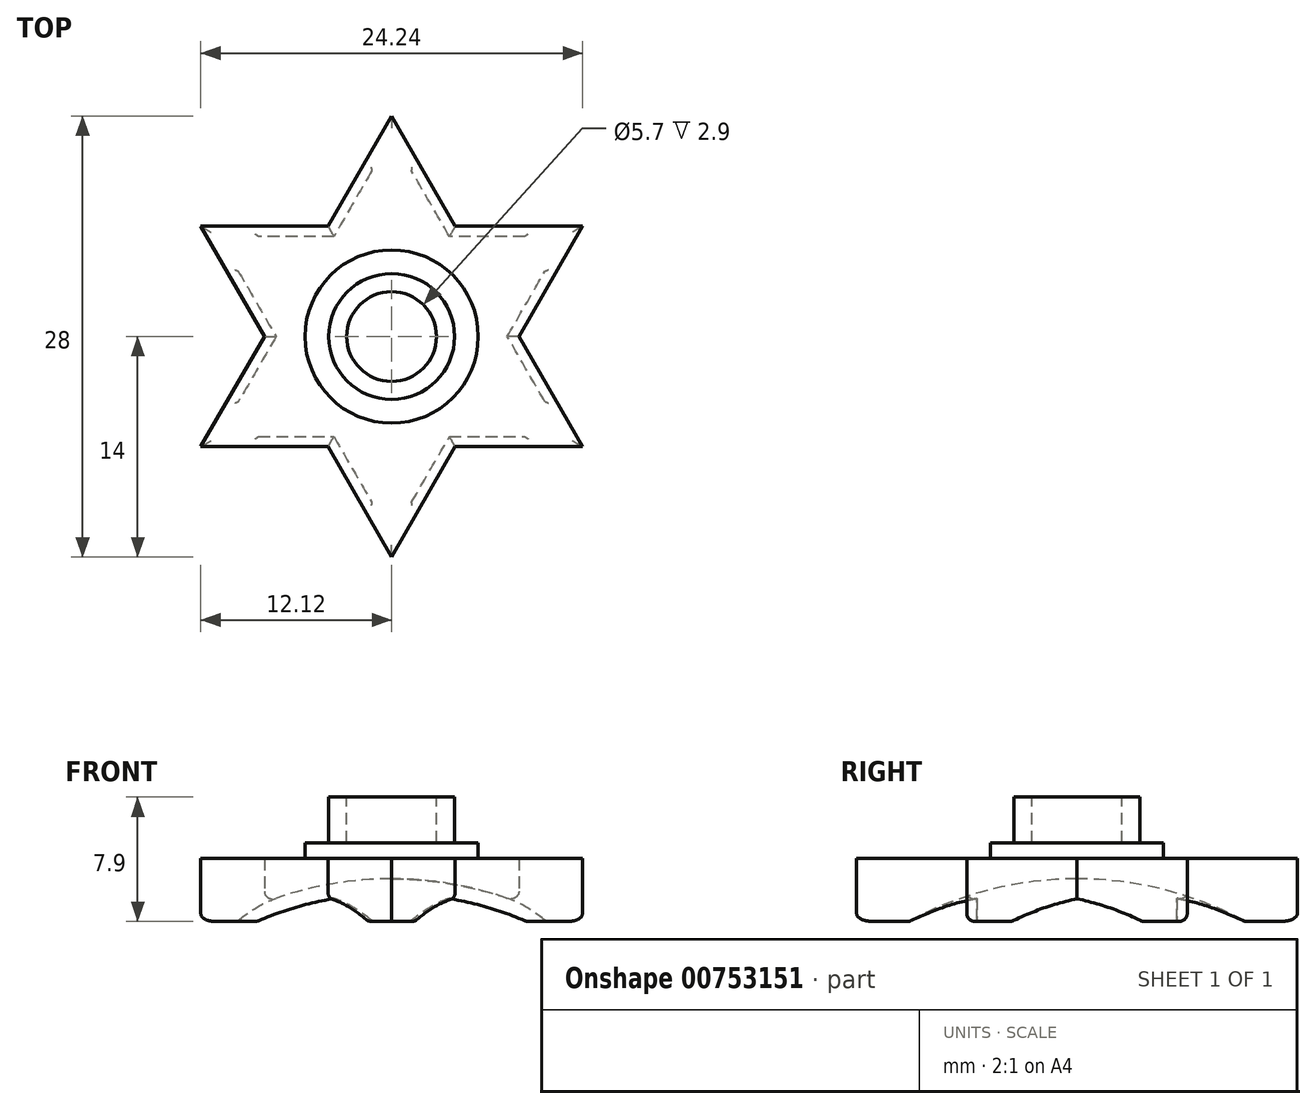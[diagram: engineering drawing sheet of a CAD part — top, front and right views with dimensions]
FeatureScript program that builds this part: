
annotation { "Feature Type Name" : "Feature", "Feature Type Description" : "" }
export const myFeature = defineFeature(function(context is Context, id is Id, definition is map)
    precondition{}
    {
        {
            var Q0;
            Q0=qCreatedBy(makeId("Top.planeOp"),FACE);
            var sketch = newSketch(context, id + "F0", { "sketchPlane" : qUnion([Q0])});
            skCircle(sketch, "E0", {"center": v(0, 0) * mm, "radius": 14 * mm, "construction": true});
            skLineSegment(sketch, "E1", {"start": v(-12.12, 7) * mm, "end": v(12.12, 7) * mm});
            skLineSegment(sketch, "E2", {"start": v(12.12, 7) * mm, "end": v(0, -14) * mm});
            skLineSegment(sketch, "E3", {"start": v(0, -14) * mm, "end": v(-12.12, 7) * mm});
            skLineSegment(sketch, "E4", {"start": v(-12.12, -7) * mm, "end": v(12.12, -7) * mm});
            skLineSegment(sketch, "E5", {"start": v(12.12, -7) * mm, "end": v(0, 14) * mm});
            skLineSegment(sketch, "E6", {"start": v(0, 14) * mm, "end": v(-12.12, -7) * mm});
            skSolve(sketch);
        }
        {
            var Q0;
            Q0=qSketchRegion(id+"F0",true);
            extrude(context, id + "F1", {"entities" : qUnion([Q0]), "depth" : 4 * mm, "offsetDistance" : 25 * mm});
        }
        {
            var Q0;
            Q0=qCreatedBy(makeId("Front.planeOp"),FACE);
            var sketch = newSketch(context, id + "F2", { "sketchPlane" : qUnion([Q0])});
            skLineSegment(sketch, "E7", {"start": v(0, 0) * mm, "end": v(0, -4.5) * mm, "construction": true});
            skSolve(sketch);
        }
        {
            var Q0;
            Q0=qCreatedBy(makeId("Front.planeOp"),FACE);
            var sketch = newSketch(context, id + "F3", { "sketchPlane" : qUnion([Q0])});
            skArc(sketch, "E8", {"start": v(0, 2.7) * mm, "mid": v(-22.55, -19.85) * mm, "end": v(0, -42.4) * mm});
            skLineSegment(sketch, "E9", {"start": v(0, 2.7) * mm, "end": v(0, -42.4) * mm});
            skPoint(sketch, "E10", {"position": v(-10.7, 0) * mm});
            skSolve(sketch);
        }
        {
            var Q0;
            Q0=qSketchRegion(id+"F3",true);
            var Q1;
            Q1=sQuery(id+"F3.wireOp",EDGE,"E9");
            revolve(context, id + "F4", {"operationType" : NewBodyOperationType.REMOVE, "surfaceOperationType" : NewSurfaceOperationType.NEW, "entities" : qUnion([Q0]), "axis" : qUnion([Q1]), "revolveType" : RevolveType.FULL, "oppositeDirection" : true});
        }
        {
            var Q0;
            Q0=makeQuery(id+"F1.opExtrude","CAP_FACE",FACE,{"disambiguationData":[OSD([sQuery(id+"F0.wireOp",EDGE,"E1"),sQuery(id+"F0.wireOp",EDGE,"E2"),sQuery(id+"F0.wireOp",EDGE,"E3"),sQuery(id+"F0.wireOp",EDGE,"E4"),sQuery(id+"F0.wireOp",EDGE,"E5"),sQuery(id+"F0.wireOp",EDGE,"E6")])],"isStart":false});
            var sketch = newSketch(context, id + "F5", { "sketchPlane" : qUnion([Q0])});
            skCircle(sketch, "E11", {"center": v(0, 0) * mm, "radius": 5.5 * mm});
            skSolve(sketch);
        }
        {
            var Q0;
            Q0=qSketchRegion(id+"F5",true);
            extrude(context, id + "F6", {"entities" : qUnion([Q0]), "operationType" : NewBodyOperationType.ADD, "depth" : 1 * mm, "offsetDistance" : 25 * mm});
        }
        {
            var Q0;
            Q0=makeQuery(id+"F6.opExtrude","CAP_FACE",FACE,{"disambiguationData":[OSD([sQuery(id+"F5.wireOp",EDGE,"E11")])],"isStart":false});
            var sketch = newSketch(context, id + "F7", { "sketchPlane" : qUnion([Q0])});
            skCircle(sketch, "E12", {"center": v(0, 0) * mm, "radius": 4 * mm});
            skSolve(sketch);
        }
        {
            var Q0;
            Q0=qSketchRegion(id+"F7",true);
            extrude(context, id + "F8", {"entities" : qUnion([Q0]), "operationType" : NewBodyOperationType.ADD, "depth" : 2.9 * mm, "offsetDistance" : 25 * mm});
        }
        {
            var Q0;
            Q0=makeQuery(id+"F8.opExtrude","CAP_FACE",FACE,{"disambiguationData":[OSD([sQuery(id+"F7.wireOp",EDGE,"E12")])],"isStart":false});
            var sketch = newSketch(context, id + "F9", { "sketchPlane" : qUnion([Q0])});
            skCircle(sketch, "E13", {"center": v(0, 0) * mm, "radius": 2.85 * mm});
            skSolve(sketch);
        }
        {
            var Q0;
            Q0=qSketchRegion(id+"F9",true);
            extrude(context, id + "F10", {"entities" : qUnion([Q0]), "operationType" : NewBodyOperationType.REMOVE, "oppositeDirection" : true, "depth" : 2.9 * mm, "offsetDistance" : 25 * mm});
        }
        {
            var Q0;
            Q0=makeQuery(id+"F1.opExtrude","CAP_EDGE",EDGE,{"disambiguationData":[OSD([sQuery(id+"F0.wireOp",EDGE,"1e846c76-ade1-459f-9f20-eea542154bc1.trimOffspring")])],"isStart":true});
            var Q1;
            Q1=makeQuery(id+"F4.boolean.opBoolean","INTERSECT",EDGE,{"disambiguationData":[OD(1.0)],"derivedFrom":[makeQuery(id+"F1.opExtrude","SWEPT_FACE",FACE,{"disambiguationData":[OSD([sQuery(id+"F0.wireOp",EDGE,"1e846c76-ade1-459f-9f20-eea542154bc1.trimOffspring")])]}),makeQuery(id+"F4.opRevolve","SWEPT_FACE",FACE,{"disambiguationData":[OSD([sQuery(id+"F3.wireOp",EDGE,"E8")])]})]});
            var Q2;
            Q2=makeQuery(id+"F4.boolean.opBoolean","INTERSECT",EDGE,{"disambiguationData":[OD(1.0)],"derivedFrom":[makeQuery(id+"F1.opExtrude","SWEPT_FACE",FACE,{"disambiguationData":[OSD([sQuery(id+"F0.wireOp",EDGE,"tKFEvPMP-PRdD-FNsb-sHzV-FJ5KZ0vE21vF")])]}),makeQuery(id+"F4.opRevolve","SWEPT_FACE",FACE,{"disambiguationData":[OSD([sQuery(id+"F3.wireOp",EDGE,"E8")])]})]});
            var Q3;
            Q3=makeQuery(id+"F1.opExtrude","CAP_EDGE",EDGE,{"disambiguationData":[OSD([sQuery(id+"F0.wireOp",EDGE,"tKFEvPMP-PRdD-FNsb-sHzV-FJ5KZ0vE21vF")])],"isStart":true});
            var Q4;
            {var subQ0=sQuery(id+"F0.wireOp",EDGE,"E6");Q4=makeQuery(id+"F1.opExtrude","CAP_EDGE",EDGE,{"disambiguationData":[OSD([subQ0]),TDD([makeQuery(id+"F0.imprint","IMPRINT",EDGE,{"disambiguationData":[TD([[makeQuery(id+"F0.imprint","INTERSECT",VERTEX,{"derivedFrom":[sQuery(id+"F0.wireOp",EDGE,"E4"),subQ0]}),1.0]])],"derivedFrom":subQ0})])],"isStart":true});}
            var Q5;
            {var subQ0=sQuery(id+"F0.wireOp",EDGE,"E4");Q5=makeQuery(id+"F1.opExtrude","CAP_EDGE",EDGE,{"disambiguationData":[OSD([subQ0]),TDD([makeQuery(id+"F0.imprint","IMPRINT",EDGE,{"disambiguationData":[TD([[makeQuery(id+"F0.imprint","INTERSECT",VERTEX,{"derivedFrom":[subQ0,sQuery(id+"F0.wireOp",EDGE,"E6")]}),-1.0]])],"derivedFrom":subQ0})])],"isStart":true});}
            var Q6;
            {var subQ0=sQuery(id+"F0.wireOp",EDGE,"E3");Q6=makeQuery(id+"F1.opExtrude","CAP_EDGE",EDGE,{"disambiguationData":[OSD([subQ0]),TDD([makeQuery(id+"F0.imprint","IMPRINT",EDGE,{"disambiguationData":[TD([[makeQuery(id+"F0.imprint","INTERSECT",VERTEX,{"derivedFrom":[sQuery(id+"F0.wireOp",EDGE,"E2"),subQ0]}),-1.0]])],"derivedFrom":subQ0})])],"isStart":true});}
            var Q7;
            {var subQ0=sQuery(id+"F0.wireOp",EDGE,"E2");Q7=makeQuery(id+"F1.opExtrude","CAP_EDGE",EDGE,{"disambiguationData":[OSD([subQ0]),TDD([makeQuery(id+"F0.imprint","IMPRINT",EDGE,{"disambiguationData":[TD([[makeQuery(id+"F0.imprint","INTERSECT",VERTEX,{"derivedFrom":[subQ0,sQuery(id+"F0.wireOp",EDGE,"E3")]}),1.0]])],"derivedFrom":subQ0})])],"isStart":true});}
            var Q8;
            {var subQ0=sQuery(id+"F0.wireOp",EDGE,"E4");Q8=makeQuery(id+"F1.opExtrude","CAP_EDGE",EDGE,{"disambiguationData":[OSD([subQ0]),TDD([makeQuery(id+"F0.imprint","IMPRINT",EDGE,{"disambiguationData":[TD([[makeQuery(id+"F0.imprint","INTERSECT",VERTEX,{"derivedFrom":[subQ0,sQuery(id+"F0.wireOp",EDGE,"E5")]}),1.0]])],"derivedFrom":subQ0})])],"isStart":true});}
            var Q9;
            {var subQ0=sQuery(id+"F0.wireOp",EDGE,"E2");Q9=makeQuery(id+"F1.opExtrude","CAP_EDGE",EDGE,{"disambiguationData":[OSD([subQ0]),TDD([makeQuery(id+"F0.imprint","IMPRINT",EDGE,{"disambiguationData":[TD([[makeQuery(id+"F0.imprint","INTERSECT",VERTEX,{"derivedFrom":[sQuery(id+"F0.wireOp",EDGE,"E1"),subQ0]}),-1.0]])],"derivedFrom":subQ0})])],"isStart":true});}
            var Q10;
            {var subQ0=sQuery(id+"F0.wireOp",EDGE,"E1");Q10=makeQuery(id+"F1.opExtrude","CAP_EDGE",EDGE,{"disambiguationData":[OSD([subQ0]),TDD([makeQuery(id+"F0.imprint","IMPRINT",EDGE,{"disambiguationData":[TD([[makeQuery(id+"F0.imprint","INTERSECT",VERTEX,{"derivedFrom":[subQ0,sQuery(id+"F0.wireOp",EDGE,"E2")]}),1.0]])],"derivedFrom":subQ0})])],"isStart":true});}
            var Q11;
            {var subQ0=sQuery(id+"F0.wireOp",EDGE,"E6");Q11=makeQuery(id+"F1.opExtrude","CAP_EDGE",EDGE,{"disambiguationData":[OSD([subQ0]),TDD([makeQuery(id+"F0.imprint","IMPRINT",EDGE,{"disambiguationData":[TD([[makeQuery(id+"F0.imprint","INTERSECT",VERTEX,{"derivedFrom":[sQuery(id+"F0.wireOp",EDGE,"E5"),subQ0]}),-1.0]])],"derivedFrom":subQ0})])],"isStart":true});}
            var Q12;
            {var subQ0=sQuery(id+"F0.wireOp",EDGE,"E1");Q12=makeQuery(id+"F1.opExtrude","CAP_EDGE",EDGE,{"disambiguationData":[OSD([subQ0]),TDD([makeQuery(id+"F0.imprint","IMPRINT",EDGE,{"disambiguationData":[TD([[makeQuery(id+"F0.imprint","INTERSECT",VERTEX,{"derivedFrom":[subQ0,sQuery(id+"F0.wireOp",EDGE,"E3")]}),-1.0]])],"derivedFrom":subQ0})])],"isStart":true});}
            var Q13;
            {var subQ0=sQuery(id+"F0.wireOp",EDGE,"E3");Q13=makeQuery(id+"F1.opExtrude","CAP_EDGE",EDGE,{"disambiguationData":[OSD([subQ0]),TDD([makeQuery(id+"F0.imprint","IMPRINT",EDGE,{"disambiguationData":[TD([[makeQuery(id+"F0.imprint","INTERSECT",VERTEX,{"derivedFrom":[sQuery(id+"F0.wireOp",EDGE,"E1"),subQ0]}),1.0]])],"derivedFrom":subQ0})])],"isStart":true});}
            var Q14;
            {var subQ0=sQuery(id+"F0.wireOp",EDGE,"E1");Q14=makeQuery(id+"F4.boolean.opBoolean","INTERSECT",EDGE,{"derivedFrom":[makeQuery(id+"F1.opExtrude","SWEPT_FACE",FACE,{"disambiguationData":[OSD([subQ0]),TDD([makeQuery(id+"F0.imprint","IMPRINT",EDGE,{"disambiguationData":[TD([[makeQuery(id+"F0.imprint","INTERSECT",VERTEX,{"derivedFrom":[subQ0,sQuery(id+"F0.wireOp",EDGE,"E3")]}),-1.0]])],"derivedFrom":subQ0})])]}),makeQuery(id+"F4.opRevolve","SWEPT_FACE",FACE,{"disambiguationData":[OSD([sQuery(id+"F3.wireOp",EDGE,"E8")])]})]});}
            var Q15;
            {var subQ0=sQuery(id+"F0.wireOp",EDGE,"E1");Q15=makeQuery(id+"F4.boolean.opBoolean","INTERSECT",EDGE,{"derivedFrom":[makeQuery(id+"F1.opExtrude","SWEPT_FACE",FACE,{"disambiguationData":[OSD([subQ0]),TDD([makeQuery(id+"F0.imprint","IMPRINT",EDGE,{"disambiguationData":[TD([[makeQuery(id+"F0.imprint","INTERSECT",VERTEX,{"derivedFrom":[subQ0,sQuery(id+"F0.wireOp",EDGE,"E2")]}),1.0]])],"derivedFrom":subQ0})])]}),makeQuery(id+"F4.opRevolve","SWEPT_FACE",FACE,{"disambiguationData":[OSD([sQuery(id+"F3.wireOp",EDGE,"E8")])]})]});}
            var Q16;
            {var subQ0=sQuery(id+"F0.wireOp",EDGE,"E2");Q16=makeQuery(id+"F4.boolean.opBoolean","INTERSECT",EDGE,{"derivedFrom":[makeQuery(id+"F1.opExtrude","SWEPT_FACE",FACE,{"disambiguationData":[OSD([subQ0]),TDD([makeQuery(id+"F0.imprint","IMPRINT",EDGE,{"disambiguationData":[TD([[makeQuery(id+"F0.imprint","INTERSECT",VERTEX,{"derivedFrom":[subQ0,sQuery(id+"F0.wireOp",EDGE,"E3")]}),1.0]])],"derivedFrom":subQ0})])]}),makeQuery(id+"F4.opRevolve","SWEPT_FACE",FACE,{"disambiguationData":[OSD([sQuery(id+"F3.wireOp",EDGE,"E8")])]})]});}
            var Q17;
            {var subQ0=sQuery(id+"F0.wireOp",EDGE,"E3");Q17=makeQuery(id+"F4.boolean.opBoolean","INTERSECT",EDGE,{"derivedFrom":[makeQuery(id+"F1.opExtrude","SWEPT_FACE",FACE,{"disambiguationData":[OSD([subQ0]),TDD([makeQuery(id+"F0.imprint","IMPRINT",EDGE,{"disambiguationData":[TD([[makeQuery(id+"F0.imprint","INTERSECT",VERTEX,{"derivedFrom":[sQuery(id+"F0.wireOp",EDGE,"E2"),subQ0]}),-1.0]])],"derivedFrom":subQ0})])]}),makeQuery(id+"F4.opRevolve","SWEPT_FACE",FACE,{"disambiguationData":[OSD([sQuery(id+"F3.wireOp",EDGE,"E8")])]})]});}
            var Q18;
            {var subQ0=sQuery(id+"F0.wireOp",EDGE,"E3");Q18=makeQuery(id+"F4.boolean.opBoolean","INTERSECT",EDGE,{"derivedFrom":[makeQuery(id+"F1.opExtrude","SWEPT_FACE",FACE,{"disambiguationData":[OSD([subQ0]),TDD([makeQuery(id+"F0.imprint","IMPRINT",EDGE,{"disambiguationData":[TD([[makeQuery(id+"F0.imprint","INTERSECT",VERTEX,{"derivedFrom":[sQuery(id+"F0.wireOp",EDGE,"E1"),subQ0]}),1.0]])],"derivedFrom":subQ0})])]}),makeQuery(id+"F4.opRevolve","SWEPT_FACE",FACE,{"disambiguationData":[OSD([sQuery(id+"F3.wireOp",EDGE,"E8")])]})]});}
            var Q19;
            {var subQ0=sQuery(id+"F0.wireOp",EDGE,"E4");Q19=makeQuery(id+"F4.boolean.opBoolean","INTERSECT",EDGE,{"derivedFrom":[makeQuery(id+"F1.opExtrude","SWEPT_FACE",FACE,{"disambiguationData":[OSD([subQ0]),TDD([makeQuery(id+"F0.imprint","IMPRINT",EDGE,{"disambiguationData":[TD([[makeQuery(id+"F0.imprint","INTERSECT",VERTEX,{"derivedFrom":[subQ0,sQuery(id+"F0.wireOp",EDGE,"E6")]}),-1.0]])],"derivedFrom":subQ0})])]}),makeQuery(id+"F4.opRevolve","SWEPT_FACE",FACE,{"disambiguationData":[OSD([sQuery(id+"F3.wireOp",EDGE,"E8")])]})]});}
            var Q20;
            {var subQ0=sQuery(id+"F0.wireOp",EDGE,"E4");Q20=makeQuery(id+"F4.boolean.opBoolean","INTERSECT",EDGE,{"derivedFrom":[makeQuery(id+"F1.opExtrude","SWEPT_FACE",FACE,{"disambiguationData":[OSD([subQ0]),TDD([makeQuery(id+"F0.imprint","IMPRINT",EDGE,{"disambiguationData":[TD([[makeQuery(id+"F0.imprint","INTERSECT",VERTEX,{"derivedFrom":[subQ0,sQuery(id+"F0.wireOp",EDGE,"E5")]}),1.0]])],"derivedFrom":subQ0})])]}),makeQuery(id+"F4.opRevolve","SWEPT_FACE",FACE,{"disambiguationData":[OSD([sQuery(id+"F3.wireOp",EDGE,"E8")])]})]});}
            var Q21;
            {var subQ0=sQuery(id+"F0.wireOp",EDGE,"E5");Q21=makeQuery(id+"F4.boolean.opBoolean","INTERSECT",EDGE,{"derivedFrom":[makeQuery(id+"F1.opExtrude","SWEPT_FACE",FACE,{"disambiguationData":[OSD([subQ0]),TDD([makeQuery(id+"F0.imprint","IMPRINT",EDGE,{"disambiguationData":[TD([[makeQuery(id+"F0.imprint","INTERSECT",VERTEX,{"derivedFrom":[sQuery(id+"F0.wireOp",EDGE,"E4"),subQ0]}),-1.0]])],"derivedFrom":subQ0})])]}),makeQuery(id+"F4.opRevolve","SWEPT_FACE",FACE,{"disambiguationData":[OSD([sQuery(id+"F3.wireOp",EDGE,"E8")])]})]});}
            var Q22;
            {var subQ0=sQuery(id+"F0.wireOp",EDGE,"E5");Q22=makeQuery(id+"F4.boolean.opBoolean","INTERSECT",EDGE,{"derivedFrom":[makeQuery(id+"F1.opExtrude","SWEPT_FACE",FACE,{"disambiguationData":[OSD([subQ0]),TDD([makeQuery(id+"F0.imprint","IMPRINT",EDGE,{"disambiguationData":[TD([[makeQuery(id+"F0.imprint","INTERSECT",VERTEX,{"derivedFrom":[subQ0,sQuery(id+"F0.wireOp",EDGE,"E6")]}),1.0]])],"derivedFrom":subQ0})])]}),makeQuery(id+"F4.opRevolve","SWEPT_FACE",FACE,{"disambiguationData":[OSD([sQuery(id+"F3.wireOp",EDGE,"E8")])]})]});}
            var Q23;
            {var subQ0=sQuery(id+"F0.wireOp",EDGE,"E6");Q23=makeQuery(id+"F4.boolean.opBoolean","INTERSECT",EDGE,{"derivedFrom":[makeQuery(id+"F1.opExtrude","SWEPT_FACE",FACE,{"disambiguationData":[OSD([subQ0]),TDD([makeQuery(id+"F0.imprint","IMPRINT",EDGE,{"disambiguationData":[TD([[makeQuery(id+"F0.imprint","INTERSECT",VERTEX,{"derivedFrom":[sQuery(id+"F0.wireOp",EDGE,"E5"),subQ0]}),-1.0]])],"derivedFrom":subQ0})])]}),makeQuery(id+"F4.opRevolve","SWEPT_FACE",FACE,{"disambiguationData":[OSD([sQuery(id+"F3.wireOp",EDGE,"E8")])]})]});}
            var Q24;
            {var subQ0=sQuery(id+"F0.wireOp",EDGE,"E6");Q24=makeQuery(id+"F4.boolean.opBoolean","INTERSECT",EDGE,{"derivedFrom":[makeQuery(id+"F1.opExtrude","SWEPT_FACE",FACE,{"disambiguationData":[OSD([subQ0]),TDD([makeQuery(id+"F0.imprint","IMPRINT",EDGE,{"disambiguationData":[TD([[makeQuery(id+"F0.imprint","INTERSECT",VERTEX,{"derivedFrom":[sQuery(id+"F0.wireOp",EDGE,"E4"),subQ0]}),1.0]])],"derivedFrom":subQ0})])]}),makeQuery(id+"F4.opRevolve","SWEPT_FACE",FACE,{"disambiguationData":[OSD([sQuery(id+"F3.wireOp",EDGE,"E8")])]})]});}
            var Q25;
            Q25=makeQuery(id+"F4.boolean.opBoolean","INTERSECT",EDGE,{"disambiguationData":[OD(1.0)],"derivedFrom":[makeQuery(id+"F1.opExtrude","CAP_FACE",FACE,{"disambiguationData":[OSD([sQuery(id+"F0.wireOp",EDGE,"E1"),sQuery(id+"F0.wireOp",EDGE,"E2"),sQuery(id+"F0.wireOp",EDGE,"E3"),sQuery(id+"F0.wireOp",EDGE,"E4"),sQuery(id+"F0.wireOp",EDGE,"E5"),sQuery(id+"F0.wireOp",EDGE,"E6")])],"isStart":true}),makeQuery(id+"F4.opRevolve","SWEPT_FACE",FACE,{"disambiguationData":[OSD([sQuery(id+"F3.wireOp",EDGE,"E8")])]})]});
            var Q26;
            Q26=makeQuery(id+"F4.boolean.opBoolean","INTERSECT",EDGE,{"disambiguationData":[OD(2.0)],"derivedFrom":[makeQuery(id+"F1.opExtrude","CAP_FACE",FACE,{"disambiguationData":[OSD([sQuery(id+"F0.wireOp",EDGE,"E1"),sQuery(id+"F0.wireOp",EDGE,"E2"),sQuery(id+"F0.wireOp",EDGE,"E3"),sQuery(id+"F0.wireOp",EDGE,"E4"),sQuery(id+"F0.wireOp",EDGE,"E5"),sQuery(id+"F0.wireOp",EDGE,"E6")])],"isStart":true}),makeQuery(id+"F4.opRevolve","SWEPT_FACE",FACE,{"disambiguationData":[OSD([sQuery(id+"F3.wireOp",EDGE,"E8")])]})]});
            var Q27;
            Q27=makeQuery(id+"F4.boolean.opBoolean","INTERSECT",EDGE,{"disambiguationData":[OD(3.0)],"derivedFrom":[makeQuery(id+"F1.opExtrude","CAP_FACE",FACE,{"disambiguationData":[OSD([sQuery(id+"F0.wireOp",EDGE,"E1"),sQuery(id+"F0.wireOp",EDGE,"E2"),sQuery(id+"F0.wireOp",EDGE,"E3"),sQuery(id+"F0.wireOp",EDGE,"E4"),sQuery(id+"F0.wireOp",EDGE,"E5"),sQuery(id+"F0.wireOp",EDGE,"E6")])],"isStart":true}),makeQuery(id+"F4.opRevolve","SWEPT_FACE",FACE,{"disambiguationData":[OSD([sQuery(id+"F3.wireOp",EDGE,"E8")])]})]});
            var Q28;
            Q28=makeQuery(id+"F4.boolean.opBoolean","INTERSECT",EDGE,{"disambiguationData":[OD(4.0)],"derivedFrom":[makeQuery(id+"F1.opExtrude","CAP_FACE",FACE,{"disambiguationData":[OSD([sQuery(id+"F0.wireOp",EDGE,"E1"),sQuery(id+"F0.wireOp",EDGE,"E2"),sQuery(id+"F0.wireOp",EDGE,"E3"),sQuery(id+"F0.wireOp",EDGE,"E4"),sQuery(id+"F0.wireOp",EDGE,"E5"),sQuery(id+"F0.wireOp",EDGE,"E6")])],"isStart":true}),makeQuery(id+"F4.opRevolve","SWEPT_FACE",FACE,{"disambiguationData":[OSD([sQuery(id+"F3.wireOp",EDGE,"E8")])]})]});
            var Q29;
            Q29=makeQuery(id+"F4.boolean.opBoolean","INTERSECT",EDGE,{"disambiguationData":[OD(5.0)],"derivedFrom":[makeQuery(id+"F1.opExtrude","CAP_FACE",FACE,{"disambiguationData":[OSD([sQuery(id+"F0.wireOp",EDGE,"E1"),sQuery(id+"F0.wireOp",EDGE,"E2"),sQuery(id+"F0.wireOp",EDGE,"E3"),sQuery(id+"F0.wireOp",EDGE,"E4"),sQuery(id+"F0.wireOp",EDGE,"E5"),sQuery(id+"F0.wireOp",EDGE,"E6")])],"isStart":true}),makeQuery(id+"F4.opRevolve","SWEPT_FACE",FACE,{"disambiguationData":[OSD([sQuery(id+"F3.wireOp",EDGE,"E8")])]})]});
            var Q30;
            {var subQ0=sQuery(id+"F0.wireOp",EDGE,"E2");Q30=makeQuery(id+"F4.boolean.opBoolean","INTERSECT",EDGE,{"derivedFrom":[makeQuery(id+"F1.opExtrude","SWEPT_FACE",FACE,{"disambiguationData":[OSD([subQ0]),TDD([makeQuery(id+"F0.imprint","IMPRINT",EDGE,{"disambiguationData":[TD([[makeQuery(id+"F0.imprint","INTERSECT",VERTEX,{"derivedFrom":[sQuery(id+"F0.wireOp",EDGE,"E1"),subQ0]}),-1.0]])],"derivedFrom":subQ0})])]}),makeQuery(id+"F4.opRevolve","SWEPT_FACE",FACE,{"disambiguationData":[OSD([sQuery(id+"F3.wireOp",EDGE,"E8")])]})]});}
            var Q31;
            {var subQ0=sQuery(id+"F0.wireOp",EDGE,"E5");Q31=makeQuery(id+"F1.opExtrude","CAP_EDGE",EDGE,{"disambiguationData":[OSD([subQ0]),TDD([makeQuery(id+"F0.imprint","IMPRINT",EDGE,{"disambiguationData":[TD([[makeQuery(id+"F0.imprint","INTERSECT",VERTEX,{"derivedFrom":[sQuery(id+"F0.wireOp",EDGE,"E4"),subQ0]}),-1.0]])],"derivedFrom":subQ0})])],"isStart":true});}
            var Q32;
            {var subQ0=sQuery(id+"F0.wireOp",EDGE,"E5");Q32=makeQuery(id+"F1.opExtrude","CAP_EDGE",EDGE,{"disambiguationData":[OSD([subQ0]),TDD([makeQuery(id+"F0.imprint","IMPRINT",EDGE,{"disambiguationData":[TD([[makeQuery(id+"F0.imprint","INTERSECT",VERTEX,{"derivedFrom":[subQ0,sQuery(id+"F0.wireOp",EDGE,"E6")]}),1.0]])],"derivedFrom":subQ0})])],"isStart":true});}
            var Q33;
            Q33=makeQuery(id+"F4.boolean.opBoolean","INTERSECT",EDGE,{"disambiguationData":[OD(0.0)],"derivedFrom":[makeQuery(id+"F1.opExtrude","CAP_FACE",FACE,{"disambiguationData":[OSD([sQuery(id+"F0.wireOp",EDGE,"E1"),sQuery(id+"F0.wireOp",EDGE,"E2"),sQuery(id+"F0.wireOp",EDGE,"E3"),sQuery(id+"F0.wireOp",EDGE,"E4"),sQuery(id+"F0.wireOp",EDGE,"E5"),sQuery(id+"F0.wireOp",EDGE,"E6")])],"isStart":true}),makeQuery(id+"F4.opRevolve","SWEPT_FACE",FACE,{"disambiguationData":[OSD([sQuery(id+"F3.wireOp",EDGE,"E8")])]})]});
            fillet(context, id + "F11", {"entities" : qUnion([Q0, Q1, Q2, Q3, Q4, Q5, Q6, Q7, Q8, Q9, Q10, Q11, Q12, Q13, Q14, Q15, Q16, Q17, Q18, Q19, Q20, Q21, Q22, Q23, Q24, Q25, Q26, Q27, Q28, Q29, Q30, Q31, Q32, Q33]), "radius" : 0.5 * mm, "tangentPropagation" : true, "allowEdgeOverflow" : false});
        }
    });
